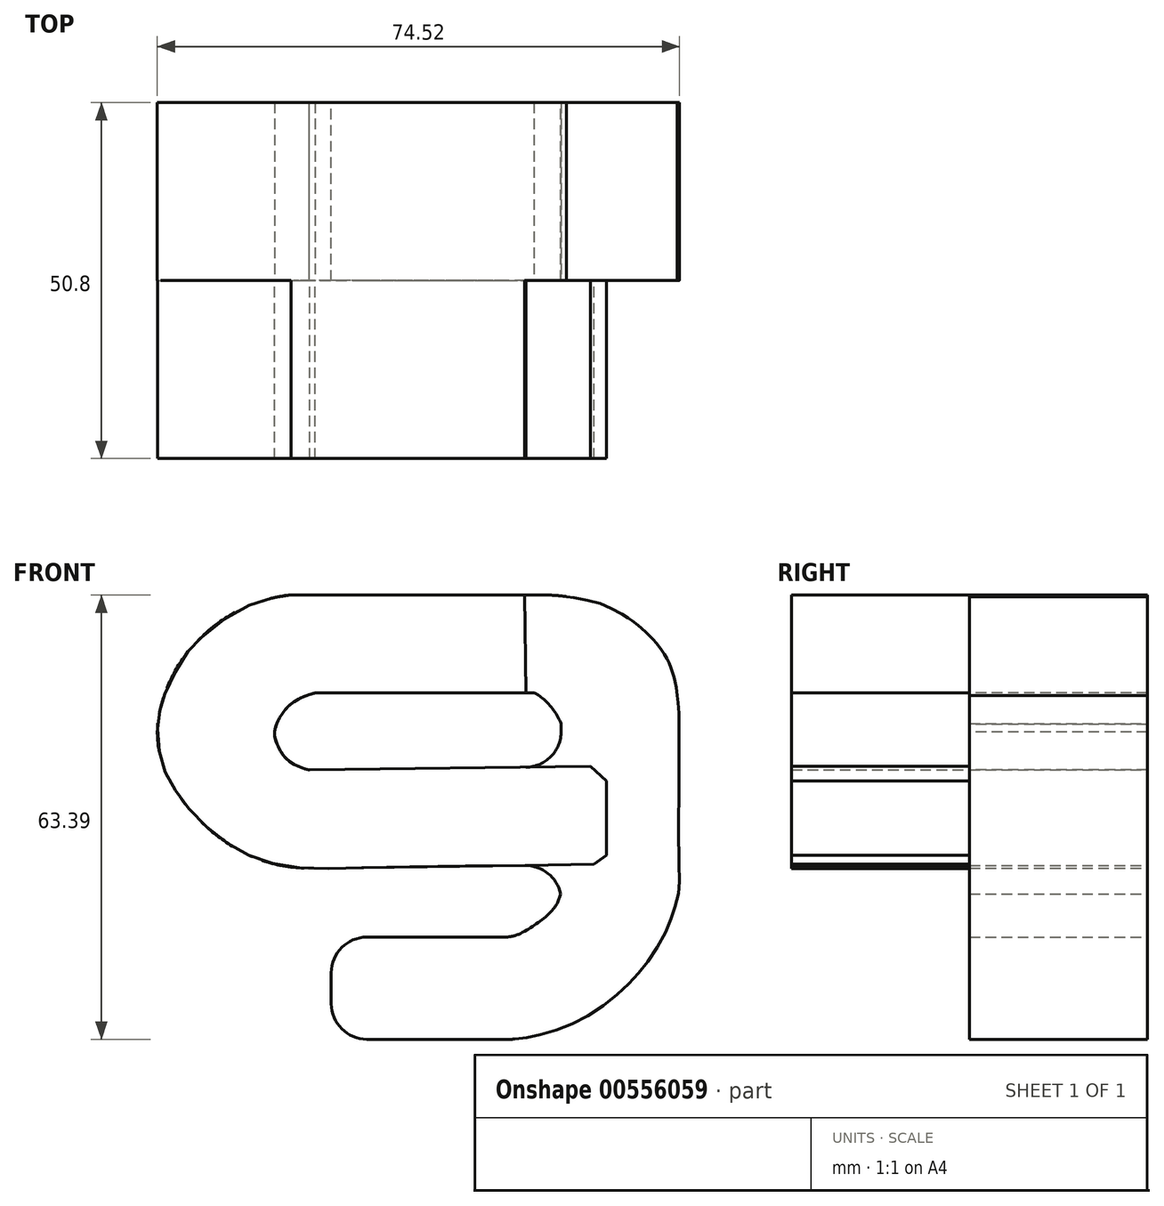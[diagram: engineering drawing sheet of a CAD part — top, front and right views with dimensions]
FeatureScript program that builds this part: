
annotation { "Feature Type Name" : "Feature", "Feature Type Description" : "" }
export const myFeature = defineFeature(function(context is Context, id is Id, definition is map)
    precondition{}
    {
        {
            var Q0;
            Q0=qCreatedBy(makeId("Front.planeOp"),FACE);
            var sketch = newSketch(context, id + "F0", { "sketchPlane" : qUnion([Q0])});
            skLineSegment(sketch, "E0", {"start": v(2.15, 6.81) * mm, "end": v(2.15, -6.54) * mm});
            skLineSegment(sketch, "E1", {"start": v(2.15, -6.54) * mm, "end": v(28.08, -6.54) * mm});
            skLineSegment(sketch, "E2", {"start": v(8.75, 56.85) * mm, "end": v(33.3, 56.85) * mm});
            skArc(sketch, "E3", {"start": v(34.97, 38.41) * mm, "mid": v(33.57, 40.87) * mm, "end": v(31.45, 42.74) * mm});
            skArc(sketch, "E4", {"start": v(-0.71, 42.76) * mm, "mid": v(-4.03, 40.92) * mm, "end": v(-5.9, 37.62) * mm});
            skArc(sketch, "E5", {"start": v(-5.9, 37.62) * mm, "mid": v(-5.9, 37.62) * mm, "end": v(-5.89, 37.62) * mm});
            skArc(sketch, "E6", {"start": v(-5.89, 37.62) * mm, "mid": v(-4.48, 33.76) * mm, "end": v(-0.82, 31.9) * mm});
            skLineSegment(sketch, "E7", {"start": v(-0.82, 31.9) * mm, "end": v(39.32, 32.4) * mm});
            skLineSegment(sketch, "E8", {"start": v(39.32, 32.4) * mm, "end": v(41.54, 30.2) * mm});
            skLineSegment(sketch, "E9", {"start": v(41.54, 30.2) * mm, "end": v(41.54, 19.66) * mm});
            skLineSegment(sketch, "E10", {"start": v(41.54, 19.66) * mm, "end": v(39.64, 18.37) * mm});
            skLineSegment(sketch, "E11", {"start": v(39.64, 18.37) * mm, "end": v(-0.82, 17.86) * mm});
            skArc(sketch, "E12", {"start": v(-11.96, 21.01) * mm, "mid": v(-6.62, 18.63) * mm, "end": v(-0.82, 17.86) * mm});
            skArc(sketch, "E13", {"start": v(-21.28, 31.05) * mm, "mid": v(-17.3, 25.4) * mm, "end": v(-11.96, 21.01) * mm});
            skArc(sketch, "E14", {"start": v(-21.78, 42.21) * mm, "mid": v(-22.67, 36.58) * mm, "end": v(-21.28, 31.05) * mm});
            skArc(sketch, "E15", {"start": v(-3.93, 56.85) * mm, "mid": v(-11.43, 54.5) * mm, "end": v(-17.58, 49.6) * mm});
            skLineSegment(sketch, "E16", {"start": v(8.75, 56.85) * mm, "end": v(-3.93, 56.85) * mm});
            skArc(sketch, "E17", {"start": v(-17.58, 49.6) * mm, "mid": v(-20.09, 46.14) * mm, "end": v(-21.78, 42.21) * mm});
            skLineSegment(sketch, "E18", {"start": v(-0.71, 42.76) * mm, "end": v(31.45, 42.74) * mm});
            skLineSegment(sketch, "E19", {"start": v(34.97, 38.41) * mm, "end": v(34.97, 13.3) * mm});
            skArc(sketch, "E20", {"start": v(27.98, 8.04) * mm, "mid": v(31.83, 10.21) * mm, "end": v(34.97, 13.3) * mm});
            skLineSegment(sketch, "E21", {"start": v(27.98, 8.04) * mm, "end": v(2.15, 8.04) * mm});
            skLineSegment(sketch, "E22", {"start": v(2.15, 8.04) * mm, "end": v(2.15, 6.81) * mm});
            skFitSpline(sketch, "E23", {"points": [v(51.53, 42.52) * mm, v(51.64, 41.6) * mm, v(51.75, 40.45) * mm, v(51.77, 18.7) * mm, v(51.77, 14.73) * mm, v(51.1, 11.97) * mm, v(50.1, 9.32) * mm, v(47.77, 5.21) * mm, v(45.49, 2.34) * mm, v(42.8, -0.33) * mm, v(38.44, -3.35) * mm, v(34.1, -5.27) * mm, v(30.34, -6.24) * mm, v(28.08, -6.54) * mm], "startDerivative": vector(2.75, -27.51) * mm, "endDerivative": vector(-36.62, -3.82) * mm});
            skFitSpline(sketch, "E24", {"points": [v(51.53, 42.52) * mm, v(51.37, 43.62) * mm, v(51.24, 44.34) * mm, v(51.16, 44.73) * mm, v(51.08, 45.03) * mm, v(50.96, 45.5) * mm, v(50.85, 45.87) * mm, v(50.84, 45.9) * mm, v(50.7, 46.3) * mm, v(50.53, 46.77) * mm, v(50.36, 47.16) * mm, v(50.2, 47.48) * mm, v(49.93, 47.99) * mm, v(49.75, 48.31) * mm, v(49.34, 48.95) * mm, v(49.05, 49.36) * mm, v(48.47, 50.1) * mm, v(48.17, 50.44) * mm, v(47.95, 50.68) * mm, v(47.58, 51.07) * mm, v(47.3, 51.34) * mm, v(47.02, 51.6) * mm, v(46.63, 51.96) * mm, v(46.25, 52.3) * mm, v(46, 52.5) * mm, v(45.22, 53.11) * mm, v(44.94, 53.32) * mm, v(44.6, 53.55) * mm, v(43.96, 53.98) * mm, v(41.82, 55.12) * mm, v(39.48, 55.96) * mm, v(36.54, 56.53) * mm, v(35.73, 56.65) * mm], "startDerivative": vector(-4.1, 27.31) * mm, "endDerivative": vector(-18.4, 2.71) * mm});
            skFitSpline(sketch, "E25", {"points": [v(35.73, 56.65) * mm, v(35.17, 56.71) * mm, v(34.95, 56.74) * mm, v(33.3, 56.85) * mm], "startDerivative": vector(-2.27, 0.29) * mm, "endDerivative": vector(-4.32, 0.12) * mm});
            skSolve(sketch);
        }
        {
            var Q0;
            {var subQ1=sQuery(id+"F0.wireOp",EDGE,"E8");Q0=makeQuery(id+"F0.imprint","IMPRINT",FACE,{"disambiguationData":[TD([[makeQuery(id+"F0.imprint","IMPRINT",EDGE,{"derivedFrom":subQ1}),-1.0]])]});}
            var Q1;
            Q1=makeQuery(id+"F0.imprint","IMPRINT",FACE,{"disambiguationData":[TD([[makeQuery(id+"F0.imprint","IMPRINT",EDGE,{"derivedFrom":sQuery(id+"F0.wireOp",EDGE,"E0")}),1.0]])]});
            extrude(context, id + "F1", {"entities" : qUnion([Q0, Q1]), "depth" : 25.4 * mm, "offsetDistance" : 25.4 * mm});
        }
        {
            var Q0;
            Q0=makeQuery(id+"F1.opExtrude","CAP_FACE",FACE,{"disambiguationData":[OSD([sQuery(id+"F0.wireOp",EDGE,"E0"),sQuery(id+"F0.wireOp",EDGE,"E1"),sQuery(id+"F0.wireOp",EDGE,"E2"),sQuery(id+"F0.wireOp",EDGE,"E11"),sQuery(id+"F0.wireOp",EDGE,"E12"),sQuery(id+"F0.wireOp",EDGE,"E13"),sQuery(id+"F0.wireOp",EDGE,"E14"),sQuery(id+"F0.wireOp",EDGE,"E15"),sQuery(id+"F0.wireOp",EDGE,"E16"),sQuery(id+"F0.wireOp",EDGE,"E17"),sQuery(id+"F0.wireOp",EDGE,"E19"),sQuery(id+"F0.wireOp",EDGE,"E20"),sQuery(id+"F0.wireOp",EDGE,"E21"),sQuery(id+"F0.wireOp",EDGE,"E22"),sQuery(id+"F0.wireOp",EDGE,"dda80a8d-c58a-43c5-84d2-bf2e6782f210"),sQuery(id+"F0.wireOp",EDGE,"2805aec2-3175-4b5c-a901-7eb59428d428"),sQuery(id+"F0.wireOp",EDGE,"eeb3e264-39d6-4b7b-ae5d-d4c4c8593c62"),sQuery(id+"F0.wireOp",EDGE,"a9fb63c2-a082-46a4-a51e-85e7194d6d4b"),sQuery(id+"F0.wireOp",EDGE,"e18e2570-d01c-4daa-ac52-c75456d3fc49.trimOffspring")])],"isStart":false});
            var sketch = newSketch(context, id + "F2", { "sketchPlane" : qUnion([Q0])});
            skLineSegment(sketch, "E26", {"start": v(35.01, 32.34) * mm, "end": v(34.94, 38.33) * mm});
            skLineSegment(sketch, "E27", {"start": v(34.94, 38.33) * mm, "end": v(34.93, 38.54) * mm});
            skLineSegment(sketch, "E28", {"start": v(31.07, 42.9) * mm, "end": v(-0.82, 42.9) * mm});
            skLineSegment(sketch, "E29", {"start": v(-5.94, 37.3) * mm, "end": v(-5.94, 36.83) * mm});
            skLineSegment(sketch, "E30", {"start": v(-1.02, 31.9) * mm, "end": v(35.01, 32.34) * mm});
            skFitSpline(sketch, "E31", {"points": [v(34.94, 38.33) * mm, v(34.93, 38.54) * mm, v(34.65, 39.19) * mm, v(34.09, 40.14) * mm, v(33.44, 41) * mm, v(32.64, 41.84) * mm, v(31.9, 42.45) * mm, v(31.46, 42.74) * mm, v(31.07, 42.9) * mm], "startDerivative": vector(0.34, 2.74) * mm, "endDerivative": vector(-4.1, 1.58) * mm});
            skFitSpline(sketch, "E32", {"points": [v(-0.7, 42.75) * mm, v(-0.2, 42.9) * mm], "startDerivative": vector(0.51, 0.15) * mm, "endDerivative": vector(0.51, 0.15) * mm});
            skFitSpline(sketch, "E33", {"points": [v(-0.7, 42.75) * mm, v(-1.43, 42.54) * mm, v(-2.5, 42.07) * mm, v(-3.6, 41.31) * mm, v(-4.28, 40.66) * mm, v(-4.96, 39.79) * mm, v(-5.54, 38.7) * mm, v(-5.88, 37.67) * mm, v(-5.94, 37.3) * mm, v(-5.94, 36.83) * mm, v(-5.62, 35.75) * mm, v(-5.3, 34.96) * mm, v(-4.7, 34.02) * mm, v(-4.01, 33.28) * mm, v(-3.08, 32.62) * mm, v(-2.48, 32.33) * mm, v(-1.9, 32.1) * mm, v(-1.02, 31.9) * mm, v(-0.99, 31.9) * mm, v(-0.64, 31.91) * mm], "startDerivative": vector(-13.6, -3.7) * mm, "endDerivative": vector(13.13, 0.04) * mm});
            skSolve(sketch);
        }
        {
            var Q0;
            Q0 = qSketchRegion(id + "F2", true);
            extrude(context, id + "F3", {"entities" : qUnion([Q0]), "operationType" : NewBodyOperationType.REMOVE, "oppositeDirection" : true, "depth" : 127 * mm, "offsetDistance" : 25.4 * mm});
        }
        {
            var Q0;
            Q0=makeQuery(id+"F1.opExtrude","SWEPT_EDGE",EDGE,{"disambiguationData":[OSD([sQuery(id+"F0.wireOp",EDGE,"E21"),sQuery(id+"F0.wireOp",EDGE,"E22")])]});
            var Q1;
            Q1=makeQuery(id+"F1.opExtrude","SWEPT_EDGE",EDGE,{"disambiguationData":[OSD([sQuery(id+"F0.wireOp",EDGE,"E0"),sQuery(id+"F0.wireOp",EDGE,"E1")])]});
            var Q2;
            Q2=makeQuery(id+"F1.opExtrude","SWEPT_EDGE",EDGE,{"disambiguationData":[OSD([sQuery(id+"F0.wireOp",EDGE,"E19"),sQuery(id+"F0.wireOp",EDGE,"E20")])]});
            var Q3;
            Q3=makeQuery(id+"F1.opExtrude","SWEPT_EDGE",EDGE,{"disambiguationData":[OSD([sQuery(id+"F0.wireOp",EDGE,"E20"),sQuery(id+"F0.wireOp",EDGE,"E21")])]});
            var Q4;
            Q4=makeQuery(id+"F1.opExtrude","SWEPT_EDGE",EDGE,{"disambiguationData":[OSD([sQuery(id+"F0.wireOp",EDGE,"E11"),sQuery(id+"F0.wireOp",EDGE,"E19")])]});
            var Q5;
            Q5=makeQuery(id+"F3.boolean.opBoolean","COPY",EDGE,{"derivedFrom":makeQuery(id+"F3.opExtrude","SWEPT_EDGE",EDGE,{"disambiguationData":[OSD([sQuery(id+"F2.wireOp",EDGE,"E26"),sQuery(id+"F2.wireOp",EDGE,"E30")])]})});
            var Q6;
            Q6=makeQuery(id+"F3.boolean.opBoolean","COPY",EDGE,{"derivedFrom":makeQuery(id+"F3.opExtrude","SWEPT_EDGE",EDGE,{"disambiguationData":[OSD([sQuery(id+"F2.wireOp",EDGE,"E30"),sQuery(id+"F2.wireOp",EDGE,"E33")])]})});
            var Q7;
            Q7=makeQuery(id+"F3.boolean.opBoolean","COPY",EDGE,{"derivedFrom":makeQuery(id+"F3.opExtrude","SWEPT_EDGE",EDGE,{"disambiguationData":[OSD([sQuery(id+"F2.wireOp",EDGE,"E26"),sQuery(id+"F2.wireOp",EDGE,"E27"),sQuery(id+"F2.wireOp",EDGE,"E31")])]})});
            var Q8;
            Q8=makeQuery(id+"F3.boolean.opBoolean","COPY",EDGE,{"derivedFrom":makeQuery(id+"F3.opExtrude","SWEPT_EDGE",EDGE,{"disambiguationData":[OSD([sQuery(id+"F2.wireOp",EDGE,"E32"),sQuery(id+"F2.wireOp",EDGE,"E33")])]})});
            var Q9;
            Q9=makeQuery(id+"F1.opExtrude","SWEPT_EDGE",EDGE,{"disambiguationData":[OSD([sQuery(id+"F0.wireOp",EDGE,"E2"),sQuery(id+"F0.wireOp",EDGE,"2805aec2-3175-4b5c-a901-7eb59428d428")])]});
            var Q10;
            Q10=makeQuery(id+"F1.opExtrude","SWEPT_EDGE",EDGE,{"disambiguationData":[OSD([sQuery(id+"F0.wireOp",EDGE,"dda80a8d-c58a-43c5-84d2-bf2e6782f210"),sQuery(id+"F0.wireOp",EDGE,"2805aec2-3175-4b5c-a901-7eb59428d428")])]});
            var Q11;
            Q11=makeQuery(id+"F1.opExtrude","SWEPT_EDGE",EDGE,{"disambiguationData":[OSD([sQuery(id+"F0.wireOp",EDGE,"dda80a8d-c58a-43c5-84d2-bf2e6782f210"),sQuery(id+"F0.wireOp",EDGE,"e18e2570-d01c-4daa-ac52-c75456d3fc49.trimOffspring")])]});
            var Q12;
            Q12=makeQuery(id+"F1.opExtrude","SWEPT_EDGE",EDGE,{"disambiguationData":[OSD([sQuery(id+"F0.wireOp",EDGE,"eeb3e264-39d6-4b7b-ae5d-d4c4c8593c62"),sQuery(id+"F0.wireOp",EDGE,"e18e2570-d01c-4daa-ac52-c75456d3fc49.trimOffspring")])]});
            var Q13;
            Q13=makeQuery(id+"F1.opExtrude","SWEPT_EDGE",EDGE,{"disambiguationData":[OSD([sQuery(id+"F0.wireOp",EDGE,"eeb3e264-39d6-4b7b-ae5d-d4c4c8593c62"),sQuery(id+"F0.wireOp",EDGE,"a9fb63c2-a082-46a4-a51e-85e7194d6d4b")])]});
            var Q14;
            Q14=makeQuery(id+"F1.opExtrude","SWEPT_EDGE",EDGE,{"disambiguationData":[OSD([sQuery(id+"F0.wireOp",EDGE,"E1"),sQuery(id+"F0.wireOp",EDGE,"a9fb63c2-a082-46a4-a51e-85e7194d6d4b")])]});
            var Q15;
            Q15=makeQuery(id+"F1.opExtrude","SWEPT_EDGE",EDGE,{"disambiguationData":[OSD([sQuery(id+"F0.wireOp",EDGE,"E13"),sQuery(id+"F0.wireOp",EDGE,"E14")])]});
            var Q16;
            Q16=makeQuery(id+"F1.opExtrude","SWEPT_EDGE",EDGE,{"disambiguationData":[OSD([sQuery(id+"F0.wireOp",EDGE,"E14"),sQuery(id+"F0.wireOp",EDGE,"E17")])]});
            var Q17;
            Q17=makeQuery(id+"F1.opExtrude","SWEPT_EDGE",EDGE,{"disambiguationData":[OSD([sQuery(id+"F0.wireOp",EDGE,"E15"),sQuery(id+"F0.wireOp",EDGE,"E17")])]});
            var Q18;
            Q18=makeQuery(id+"F1.opExtrude","SWEPT_EDGE",EDGE,{"disambiguationData":[OSD([sQuery(id+"F0.wireOp",EDGE,"E15"),sQuery(id+"F0.wireOp",EDGE,"E16")])]});
            var Q19;
            Q19=makeQuery(id+"F1.opExtrude","SWEPT_EDGE",EDGE,{"disambiguationData":[OSD([sQuery(id+"F0.wireOp",EDGE,"E12"),sQuery(id+"F0.wireOp",EDGE,"E13")])]});
            var Q20;
            Q20=makeQuery(id+"F1.opExtrude","SWEPT_EDGE",EDGE,{"disambiguationData":[OSD([sQuery(id+"F0.wireOp",EDGE,"E11"),sQuery(id+"F0.wireOp",EDGE,"E12")])]});
            fillet(context, id + "F4", {"entities" : qUnion([Q0, Q1, Q2, Q3, Q4, Q5, Q6, Q7, Q8, Q9, Q10, Q11, Q12, Q13, Q14, Q15, Q16, Q17, Q18, Q19, Q20]), "radius" : 5.08 * mm, "tangentPropagation" : true, "allowEdgeOverflow" : false});
        }
        {
            var Q0;
            Q0=makeQuery(id+"F1.opExtrude","CAP_FACE",FACE,{"disambiguationData":[OSD([sQuery(id+"F0.wireOp",EDGE,"E0"),sQuery(id+"F0.wireOp",EDGE,"E1"),sQuery(id+"F0.wireOp",EDGE,"E2"),sQuery(id+"F0.wireOp",EDGE,"E11"),sQuery(id+"F0.wireOp",EDGE,"E12"),sQuery(id+"F0.wireOp",EDGE,"E13"),sQuery(id+"F0.wireOp",EDGE,"E14"),sQuery(id+"F0.wireOp",EDGE,"E15"),sQuery(id+"F0.wireOp",EDGE,"E16"),sQuery(id+"F0.wireOp",EDGE,"E17"),sQuery(id+"F0.wireOp",EDGE,"E19"),sQuery(id+"F0.wireOp",EDGE,"E20"),sQuery(id+"F0.wireOp",EDGE,"E21"),sQuery(id+"F0.wireOp",EDGE,"E22"),sQuery(id+"F0.wireOp",EDGE,"dda80a8d-c58a-43c5-84d2-bf2e6782f210"),sQuery(id+"F0.wireOp",EDGE,"2805aec2-3175-4b5c-a901-7eb59428d428"),sQuery(id+"F0.wireOp",EDGE,"eeb3e264-39d6-4b7b-ae5d-d4c4c8593c62"),sQuery(id+"F0.wireOp",EDGE,"a9fb63c2-a082-46a4-a51e-85e7194d6d4b"),sQuery(id+"F0.wireOp",EDGE,"e18e2570-d01c-4daa-ac52-c75456d3fc49.trimOffspring")])],"isStart":false});
            var sketch = newSketch(context, id + "F5", { "sketchPlane" : qUnion([Q0])});
            skLineSegment(sketch, "E34", {"start": v(29.93, 32.28) * mm, "end": v(39.11, 32.4) * mm});
            skLineSegment(sketch, "E35", {"start": v(39.11, 32.4) * mm, "end": v(41.43, 30.36) * mm});
            skLineSegment(sketch, "E36", {"start": v(41.43, 30.36) * mm, "end": v(41.43, 19.75) * mm});
            skLineSegment(sketch, "E37", {"start": v(41.43, 19.75) * mm, "end": v(39.68, 18.48) * mm});
            skLineSegment(sketch, "E38", {"start": v(39.68, 18.48) * mm, "end": v(29.83, 18.25) * mm});
            skLineSegment(sketch, "E39", {"start": v(25.26, 56.85) * mm, "end": v(-3.6, 56.85) * mm});
            skFitSpline(sketch, "E40", {"points": [v(-3.6, 56.85) * mm, v(-6.67, 56.34) * mm, v(-11.57, 54.41) * mm, v(-16.85, 50.4) * mm, v(-18.7, 48.25) * mm, v(-21.3, 43.6) * mm, v(-22.2, 40.92) * mm, v(-22.61, 38.61) * mm, v(-22.44, 34.58) * mm, v(-21.33, 31.16) * mm, v(-19.43, 28) * mm, v(-16.37, 24.44) * mm, v(-11.94, 21) * mm, v(-7.73, 18.98) * mm, v(-1.77, 17.87) * mm, v(6.5, 17.95) * mm, v(29.83, 18.25) * mm], "startDerivative": vector(-60.47, -8.47) * mm, "endDerivative": vector(198.88, 1.27) * mm});
            skLineSegment(sketch, "E41", {"start": v(29.93, 42.9) * mm, "end": v(29.76, 56.85) * mm});
            skLineSegment(sketch, "E42", {"start": v(29.76, 56.85) * mm, "end": v(25.26, 56.85) * mm});
            skLineSegment(sketch, "E43", {"start": v(29.93, 42.9) * mm, "end": v(-0.2, 42.9) * mm});
            skFitSpline(sketch, "E44", {"points": [v(-0.2, 42.9) * mm, v(-3.24, 41.6) * mm, v(-5.22, 39.36) * mm, v(-5.95, 36.97) * mm, v(-5, 34.47) * mm, v(-3.45, 32.85) * mm, v(-1, 31.9) * mm, v(-0.9, 31.9) * mm], "startDerivative": vector(-18.21, -5.87) * mm, "endDerivative": vector(2.11, 0.55) * mm});
            skLineSegment(sketch, "E45", {"start": v(-0.9, 31.9) * mm, "end": v(29.93, 32.28) * mm});
            skSolve(sketch);
        }
        {
            var Q0;
            Q0 = qSketchRegion(id + "F5", true);
            extrude(context, id + "F6", {"entities" : qUnion([Q0]), "operationType" : NewBodyOperationType.ADD, "depth" : 25.4 * mm, "offsetDistance" : 25.4 * mm});
        }
    });
